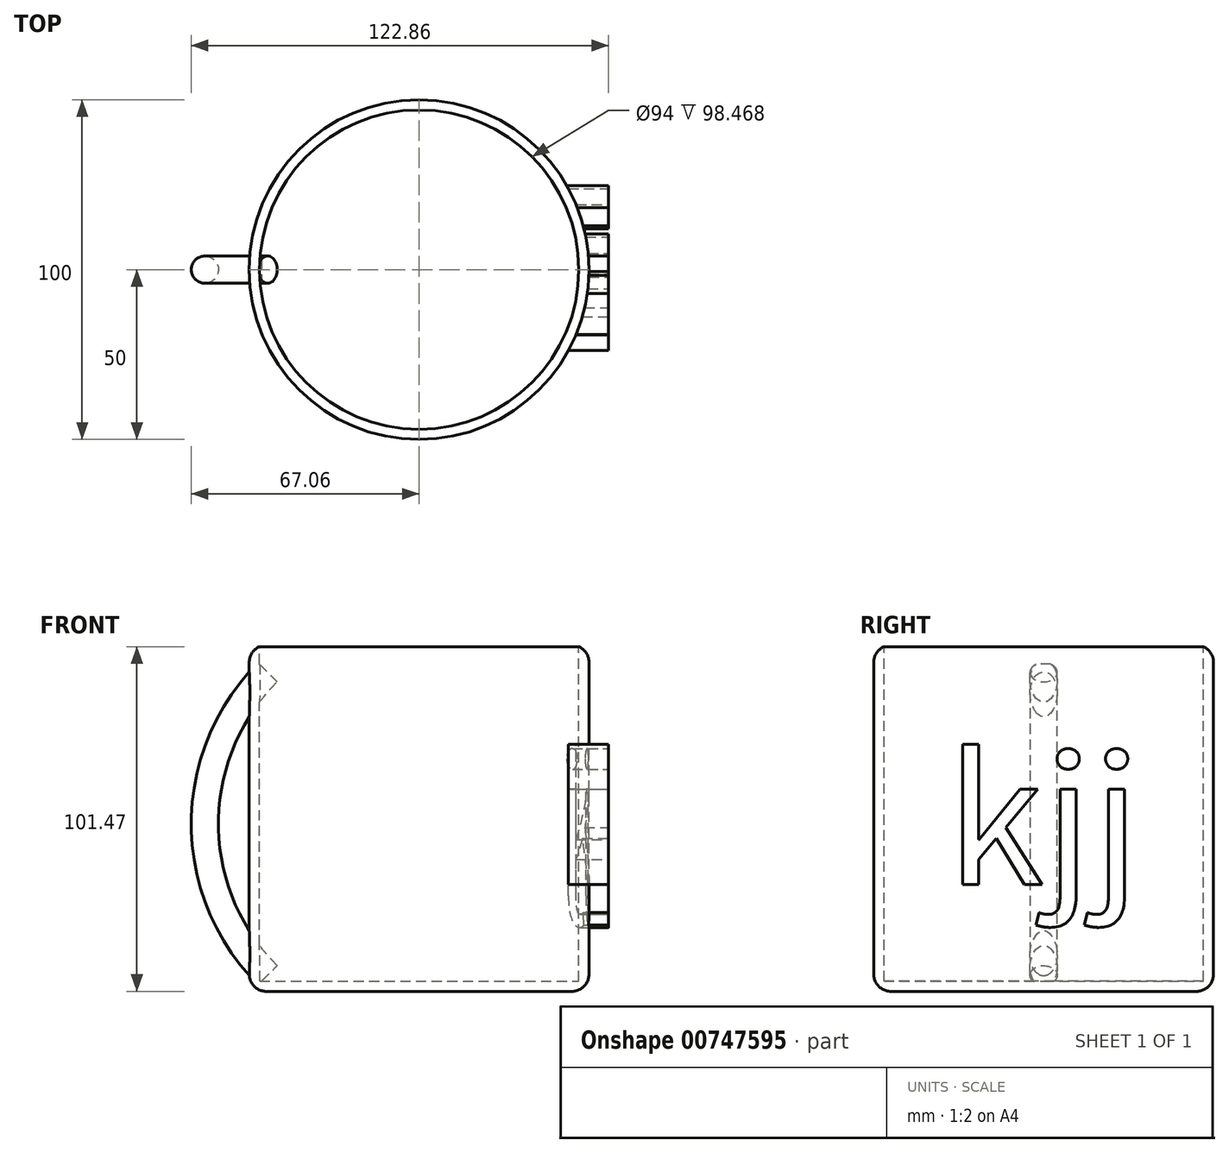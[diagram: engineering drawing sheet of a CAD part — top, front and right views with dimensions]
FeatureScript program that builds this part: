
annotation { "Feature Type Name" : "Feature", "Feature Type Description" : "" }
export const myFeature = defineFeature(function(context is Context, id is Id, definition is map)
    precondition{}
    {
        {
            var Q0;
            Q0=qCreatedBy(makeId("Right.planeOp"),FACE);
            var sketch = newSketch(context, id + "F0", { "sketchPlane" : qUnion([Q0])});
            skLineSegment(sketch, "E0", {"start": v(47, 52.14) * mm, "end": v(50, 52.14) * mm});
            skLineSegment(sketch, "E1", {"start": v(0, -49.33) * mm, "end": v(45, -49.33) * mm});
            skLineSegment(sketch, "E2", {"start": v(50, 52.14) * mm, "end": v(50, -44.33) * mm});
            skLineSegment(sketch, "E3.0", {"start": v(0, -46.33) * mm, "end": v(47, -46.33) * mm});
            skLineSegment(sketch, "E3.1", {"start": v(47, 52.14) * mm, "end": v(47, -46.33) * mm});
            skPoint(sketch, "E4.orphan", {"position": v(0, 52.14) * mm});
            skLineSegment(sketch, "E5", {"start": v(0, 52.14) * mm, "end": v(0, 0) * mm});
            skLineSegment(sketch, "E6", {"start": v(0, -46.33) * mm, "end": v(0, -49.33) * mm});
            skPoint(sketch, "E7.visualSharp", {"position": v(50, -49.33) * mm});
            skArc(sketch, "E7.filletArc", {"start": v(45, -49.33) * mm, "mid": v(48.54, -47.86) * mm, "end": v(50, -44.33) * mm});
            skSolve(sketch);
        }
        {
            var Q0;
            Q0=makeQuery(id+"F0.imprint","IMPRINT",FACE,{"disambiguationData":[TD([[makeQuery(id+"F0.imprint","IMPRINT",EDGE,{"derivedFrom":sQuery(id+"F0.wireOp",EDGE,"E0")}),-1.0]])]});
            var Q1;
            Q1=sQuery(id+"F0.wireOp",EDGE,"E5");
            revolve(context, id + "F1", {"surfaceOperationType" : NewSurfaceOperationType.NEW, "entities" : qUnion([Q0]), "axis" : qUnion([Q1]), "revolveType" : RevolveType.FULL});
        }
        {
            var Q0;
            Q0=makeQuery(id+"F1.opRevolve","SWEPT_EDGE",EDGE,{"disambiguationData":[OSD([sQuery(id+"F0.wireOp",EDGE,"E0"),sQuery(id+"F0.wireOp",EDGE,"E2")])]});
            fillet(context, id + "F2", {"entities" : qUnion([Q0]), "radius" : 5 * mm, "tangentPropagation" : true, "allowEdgeOverflow" : false});
        }
        {
            var Q0;
            Q0=qCreatedBy(makeId("Right.planeOp"),FACE);
            cPlane(context, id + "F3", {"entities" : qUnion([Q0]), "cplaneType" : CPlaneType.OFFSET, "offset" : 55.8 * mm, "width" : 150 * mm, "height" : 150 * mm});
        }
        {
            var Q0;
            Q0=qCreatedBy(id+"F3.planeOp",FACE);
            var sketch = newSketch(context, id + "F4", { "sketchPlane" : qUnion([Q0])});
            skText(sketch, "E8", { "text": "kjj", "fontName": "NotoSansCJKjp-Regular.otf"});
            const initialGuessF4  = {"E8": [-0.0286, -0.01793, 1, 0, 0.03733]};
            skSetInitialGuess(sketch, initialGuessF4);
            skSolve(sketch);
        }
        {
            var Q0;
            Q0 = qSketchRegion(id + "F4", true);
            extrude(context, id + "F5", {"entities" : qUnion([Q0]), "operationType" : NewBodyOperationType.ADD, "endBound" : BoundingType.UP_TO_NEXT, "oppositeDirection" : true, "depth" : 41.9 * mm, "offsetDistance" : 25 * mm});
        }
        {
            var Q0;
            Q0=qCreatedBy(makeId("Top.planeOp"),FACE);
            var sketch = newSketch(context, id + "F6", { "sketchPlane" : qUnion([Q0])});
            skCircle(sketch, "E9", {"center": v(-63.07, 0) * mm, "radius": 4 * mm});
            skLineSegment(sketch, "E10", {"start": v(0, 0) * mm, "end": v(0, -37.17) * mm});
            skSolve(sketch);
        }
        {
            var Q0;
            Q0=makeQuery(id+"F6.imprint","IMPRINT",FACE,{"disambiguationData":[TD([[makeQuery(id+"F6.imprint","IMPRINT",EDGE,{"derivedFrom":sQuery(id+"F6.wireOp",EDGE,"E9")}),1.0]])]});
            var Q1;
            Q1=sQuery(id+"F6.wireOp",EDGE,"E10");
            revolve(context, id + "F7", {"operationType" : NewBodyOperationType.ADD, "surfaceOperationType" : NewSurfaceOperationType.NEW, "entities" : qUnion([Q0]), "axis" : qUnion([Q1]), "revolveType" : RevolveType.TWO_DIRECTIONS, "angle" : 45 * degree, "angleBack" : 315 * degree});
        }
    });
